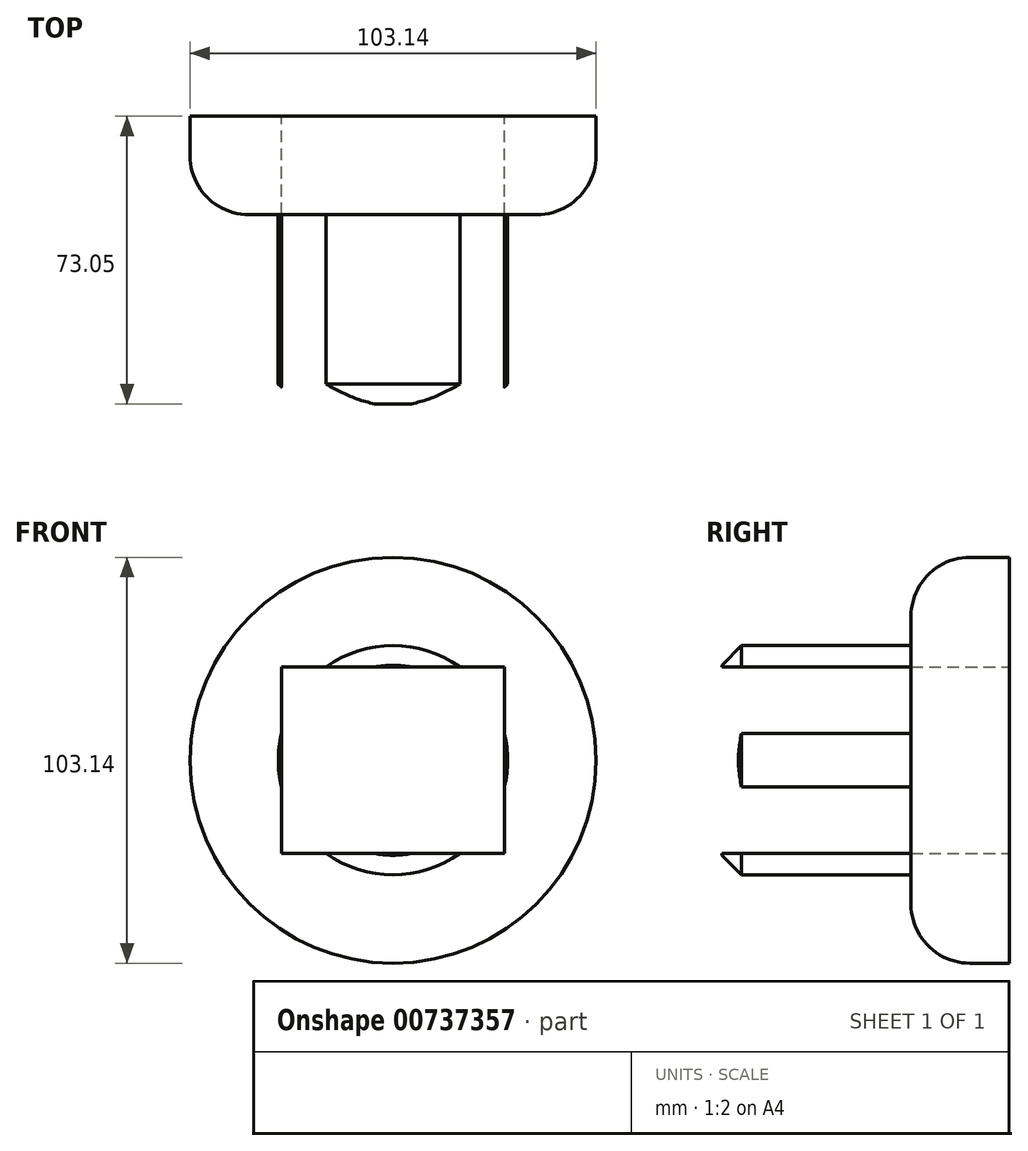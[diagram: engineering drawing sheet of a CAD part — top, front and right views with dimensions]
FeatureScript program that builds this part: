
annotation { "Feature Type Name" : "Feature", "Feature Type Description" : "" }
export const myFeature = defineFeature(function(context is Context, id is Id, definition is map)
    precondition{}
    {
        {
            var Q0;
            Q0=qCreatedBy(makeId("Front.planeOp"),FACE);
            var sketch = newSketch(context, id + "F0", { "sketchPlane" : qUnion([Q0])});
            skCircle(sketch, "E0", {"center": v(0, 0) * mm, "radius": 29.13 * mm});
            skSolve(sketch);
        }
        {
            var Q0;
            Q0=qCreatedBy(makeId("Front.planeOp"),FACE);
            var sketch = newSketch(context, id + "F1", { "sketchPlane" : qUnion([Q0])});
            skCircle(sketch, "E1", {"center": v(0, 0) * mm, "radius": 51.57 * mm});
            skSolve(sketch);
        }
        {
            var Q0;
            Q0=makeQuery(id+"F1.imprint","IMPRINT",FACE,{"disambiguationData":[TD([[makeQuery(id+"F1.imprint","IMPRINT",EDGE,{"derivedFrom":sQuery(id+"F1.wireOp",EDGE,"E1")}),1.0]])]});
            extrude(context, id + "F2", {"entities" : qUnion([Q0]), "depth" : 25 * mm, "offsetDistance" : 25 * mm});
        }
        {
            var Q0;
            Q0 = qSketchRegion(id + "F0", true);
            extrude(context, id + "F3", {"entities" : qUnion([Q0]), "operationType" : NewBodyOperationType.ADD, "depth" : 73.05 * mm, "offsetDistance" : 25 * mm});
        }
        {
            var Q0;
            Q0=makeQuery(id+"F3.opExtrude","CAP_EDGE",EDGE,{"disambiguationData":[OSD([sQuery(id+"F0.wireOp",EDGE,"E0")])],"isStart":false});
            chamfer(context, id + "F4", {"entities" : qUnion([Q0]), "width" : 5 * mm, "tangentPropagation" : true});
        }
        {
            var Q0;
            Q0=makeQuery(id+"F2.opExtrude","CAP_EDGE",EDGE,{"disambiguationData":[OSD([sQuery(id+"F1.wireOp",EDGE,"E1")])],"isStart":false});
            fillet(context, id + "F5", {"entities" : qUnion([Q0]), "radius" : 15 * mm, "tangentPropagation" : true, "allowEdgeOverflow" : false});
        }
        {
            var Q0;
            Q0=makeQuery(id+"F2.opExtrude","CAP_FACE",FACE,{"disambiguationData":[OSD([sQuery(id+"F1.wireOp",EDGE,"E1")])],"isStart":true});
            var sketch = newSketch(context, id + "F6", { "sketchPlane" : qUnion([Q0])});
            skLineSegment(sketch, "E2.bottom", {"start": v(-28.33, 23.67) * mm, "end": v(28.33, 23.67) * mm});
            skLineSegment(sketch, "E2.top", {"start": v(-28.33, -23.67) * mm, "end": v(28.33, -23.67) * mm});
            skLineSegment(sketch, "E2.left", {"start": v(-28.33, 23.67) * mm, "end": v(-28.33, -23.67) * mm});
            skLineSegment(sketch, "E2.right", {"start": v(28.33, 23.67) * mm, "end": v(28.33, -23.67) * mm});
            skPoint(sketch, "E2.middle", {"position": v(0, 0) * mm});
            skSolve(sketch);
        }
        {
            var Q0;
            Q0 = qSketchRegion(id + "F6", true);
            extrude(context, id + "F7", {"entities" : qUnion([Q0]), "operationType" : NewBodyOperationType.REMOVE, "oppositeDirection" : true, "depth" : 91.2 * mm, "offsetDistance" : 25 * mm});
        }
    });
